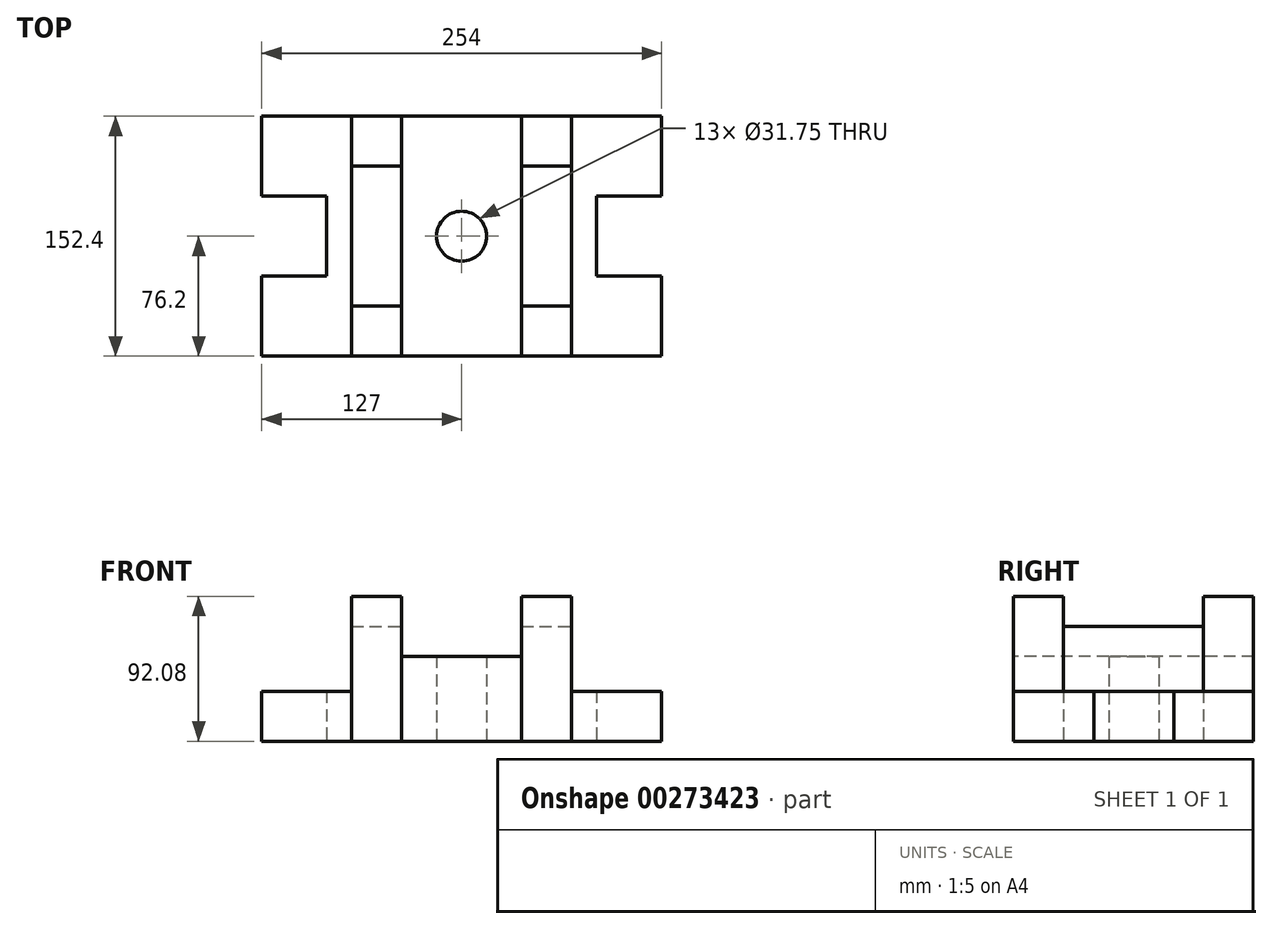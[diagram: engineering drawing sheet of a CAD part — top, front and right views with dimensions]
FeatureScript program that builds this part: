
annotation { "Feature Type Name" : "Feature", "Feature Type Description" : "" }
export const myFeature = defineFeature(function(context is Context, id is Id, definition is map)
    precondition{}
    {
        {
            var Q0;
            Q0=qCreatedBy(makeId("Top.planeOp"),FACE);
            var sketch = newSketch(context, id + "F0", { "sketchPlane" : qUnion([Q0])});
            skLineSegment(sketch, "E0.bottom", {"start": v(-38.1, 76.2) * mm, "end": v(38.1, 76.2) * mm});
            skLineSegment(sketch, "E0.top", {"start": v(-38.1, -76.2) * mm, "end": v(38.1, -76.2) * mm});
            skLineSegment(sketch, "E0.left", {"start": v(-38.1, 76.2) * mm, "end": v(-38.1, -76.2) * mm});
            skLineSegment(sketch, "E0.right", {"start": v(38.1, 76.2) * mm, "end": v(38.1, -76.2) * mm});
            skPoint(sketch, "E0.middle", {"position": v(0, 0) * mm});
            skLineSegment(sketch, "E1.bottom", {"start": v(38.1, 76.2) * mm, "end": v(69.85, 76.2) * mm});
            skLineSegment(sketch, "E1.top", {"start": v(38.1, -76.2) * mm, "end": v(69.85, -76.2) * mm});
            skLineSegment(sketch, "E1.right", {"start": v(69.85, 76.2) * mm, "end": v(69.85, -76.2) * mm});
            skLineSegment(sketch, "E2.bottom", {"start": v(-38.1, 76.2) * mm, "end": v(-69.85, 76.2) * mm});
            skLineSegment(sketch, "E2.top", {"start": v(-38.1, -76.2) * mm, "end": v(-69.85, -76.2) * mm});
            skLineSegment(sketch, "E2.right", {"start": v(-69.85, 76.2) * mm, "end": v(-69.85, -76.2) * mm});
            skLineSegment(sketch, "E3.bottom", {"start": v(69.85, 76.2) * mm, "end": v(127, 76.2) * mm});
            skLineSegment(sketch, "E3.top", {"start": v(69.85, -76.2) * mm, "end": v(127, -76.2) * mm});
            skLineSegment(sketch, "E3.right", {"start": v(127, 76.2) * mm, "end": v(127, 25.4) * mm});
            skLineSegment(sketch, "E4.bottom", {"start": v(-69.85, 76.2) * mm, "end": v(-127, 76.2) * mm});
            skLineSegment(sketch, "E4.top", {"start": v(-69.85, -76.2) * mm, "end": v(-127, -76.2) * mm});
            skLineSegment(sketch, "E4.right", {"start": v(-127, 76.2) * mm, "end": v(-127, 25.4) * mm});
            skPoint(sketch, "E5", {"position": v(-127, 25.4) * mm});
            skPoint(sketch, "E6", {"position": v(-127, -25.4) * mm});
            skPoint(sketch, "E7", {"position": v(127, 25.4) * mm});
            skPoint(sketch, "E8", {"position": v(127, -25.4) * mm});
            skLineSegment(sketch, "E9.trimOffspring", {"start": v(-127, -25.4) * mm, "end": v(-127, -76.2) * mm});
            skLineSegment(sketch, "E10.trimOffspring", {"start": v(127, -25.4) * mm, "end": v(127, -76.2) * mm});
            skLineSegment(sketch, "E11", {"start": v(-127, 25.4) * mm, "end": v(-85.73, 25.4) * mm});
            skLineSegment(sketch, "E12", {"start": v(-85.73, 25.4) * mm, "end": v(-85.73, -25.4) * mm});
            skLineSegment(sketch, "E13", {"start": v(-85.73, -25.4) * mm, "end": v(-127, -25.4) * mm});
            skLineSegment(sketch, "E14", {"start": v(127, -25.4) * mm, "end": v(85.73, -25.4) * mm});
            skLineSegment(sketch, "E15", {"start": v(85.73, -25.4) * mm, "end": v(85.72, 25.4) * mm});
            skLineSegment(sketch, "E16", {"start": v(85.72, 25.4) * mm, "end": v(127, 25.4) * mm});
            skLineSegment(sketch, "E17", {"start": v(-69.85, 44.45) * mm, "end": v(-38.1, 44.45) * mm});
            skLineSegment(sketch, "E18", {"start": v(-69.85, -44.45) * mm, "end": v(-38.1, -44.45) * mm});
            skLineSegment(sketch, "E19", {"start": v(38.1, 44.45) * mm, "end": v(69.85, 44.45) * mm});
            skLineSegment(sketch, "E20", {"start": v(38.1, -44.45) * mm, "end": v(69.85, -44.45) * mm});
            skCircle(sketch, "E21", {"center": v(0, 0) * mm, "radius": 15.88 * mm});
            skSolve(sketch);
        }
        {
            var Q0;
            Q0=makeQuery(id+"F0.imprint","IMPRINT",FACE,{"disambiguationData":[TD([[makeQuery(id+"F0.imprint","IMPRINT",EDGE,{"derivedFrom":sQuery(id+"F0.wireOp",EDGE,"E4.bottom")}),1.0]])]});
            var Q1;
            Q1=makeQuery(id+"F0.imprint","IMPRINT",FACE,{"disambiguationData":[TD([[makeQuery(id+"F0.imprint","IMPRINT",EDGE,{"derivedFrom":sQuery(id+"F0.wireOp",EDGE,"E3.bottom")}),-1.0]])]});
            extrude(context, id + "F1", {"entities" : qUnion([Q0, Q1]), "depth" : 31.75 * mm});
        }
        {
            var Q0;
            {var subQ0=sQuery(id+"F0.wireOp",EDGE,"E2.bottom");Q0=makeQuery(id+"F0.imprint","IMPRINT",FACE,{"disambiguationData":[TD([[makeQuery(id+"F0.imprint","IMPRINT",EDGE,{"derivedFrom":subQ0}),1.0]])]});}
            var Q1;
            {var subQ0=sQuery(id+"F0.wireOp",EDGE,"E2.top");Q1=makeQuery(id+"F0.imprint","IMPRINT",FACE,{"disambiguationData":[TD([[makeQuery(id+"F0.imprint","IMPRINT",EDGE,{"derivedFrom":subQ0}),-1.0]])]});}
            var Q2;
            {var subQ0=sQuery(id+"F0.wireOp",EDGE,"E1.bottom");Q2=makeQuery(id+"F0.imprint","IMPRINT",FACE,{"disambiguationData":[TD([[makeQuery(id+"F0.imprint","IMPRINT",EDGE,{"derivedFrom":subQ0}),-1.0]])]});}
            var Q3;
            {var subQ0=sQuery(id+"F0.wireOp",EDGE,"E1.top");Q3=makeQuery(id+"F0.imprint","IMPRINT",FACE,{"disambiguationData":[TD([[makeQuery(id+"F0.imprint","IMPRINT",EDGE,{"derivedFrom":subQ0}),1.0]])]});}
            extrude(context, id + "F2", {"entities" : qUnion([Q0, Q1, Q2, Q3]), "depth" : 92.07 * mm});
        }
        {
            var Q0;
            {var subQ0=sQuery(id+"F0.wireOp",EDGE,"E17");Q0=makeQuery(id+"F0.imprint","IMPRINT",FACE,{"disambiguationData":[TD([[makeQuery(id+"F0.imprint","IMPRINT",EDGE,{"derivedFrom":subQ0}),-1.0]])]});}
            var Q1;
            {var subQ0=sQuery(id+"F0.wireOp",EDGE,"E19");Q1=makeQuery(id+"F0.imprint","IMPRINT",FACE,{"disambiguationData":[TD([[makeQuery(id+"F0.imprint","IMPRINT",EDGE,{"derivedFrom":subQ0}),-1.0]])]});}
            extrude(context, id + "F3", {"entities" : qUnion([Q0, Q1]), "depth" : 73.02 * mm});
        }
        {
            var Q0;
            {var subQ3=sQuery(id+"F0.wireOp",EDGE,"E0.bottom");Q0=makeQuery(id+"F0.imprint","IMPRINT",FACE,{"disambiguationData":[TD([[makeQuery(id+"F0.imprint","IMPRINT",EDGE,{"derivedFrom":subQ3}),-1.0]])]});}
            extrude(context, id + "F4", {"entities" : qUnion([Q0]), "depth" : 53.97 * mm});
        }
    });
